# Revit family: BC_Hitachi_RAS-8-12FSXNME_LOD400
name_source: partatom
category: Equipement de génie climatique
revit_build: Autodesk Revit 2017 (Build: 20160225_1515(x64)
units: mm (PartAtom-declared; Revit-internal decimal feet)

## family parameters
Basée sur le plan de construction = Non
Cote de connecteur circulaire = Utiliser le diamètre
Couper avec des vides une fois chargée = Non
Numéro OmniClass = 23.75.00.00
Partagée = Non
Point de calcul de pièce = Non
Titre OmniClass = Climate Control (HVAC)
Toujours verticalement = Oui
Type d'élément = Normal

## types (3) — shared parameters
Approximate Packing Volume = 1.03 m³
Color = Natural Grey (1.0Y8.5/0.5)
Compressor Quantity = 1
Compressor Type = Hermetic (Scroll)
Condenser Fan Quantity = 2
Condenser Fan Type = Propeller Fan
Fabricant = Hitachi Air Conditioning Europe SAS
Flow Control = Micro-Computer control expansion valve
Frequency = 50 Hz
Heat Exchanger = Multi Pass Cross - Finned Tube
Modèle = Set Free Mini - RAS-8-12 FSXNME
Motor - Number of Poles = 6
Nominal Static Pressure = 30.0 Pa
Nominal Voltage = 400 V
Number of Poles = 3
Overall Depth = 390.00 mm
Overall Height = 1650.00 mm
Overall Width = 1100.00 mm
Packing dimensions (H x W x D) = 1787 mm x 1151 mm x 500 mm
Refrigerant Type = R410A
Refrigerant charge before shipment = 4.20 kg
Refrigeration Oil Charge = 6
Refrigeration Oil Type = FVC68D

## per-type parameters (varying)
| type | Compressor Model | Cooling Capacity | Gas Diameter | Gross Weight | Heating Capacity | Liquid Diameter | Motor power | Net Weight | Nominal Air Flow | Sound Pressure Level (night mode) | Sound level |
| RAS-8FSXNME | AA50PHD | 22 kW | 19.05 mm | 197.00 kg | 25 kW | 9.52 mm | 3 kW | 188.00 kg | 9900.0 m³/h | 55 (50) | 76 |
| RAS-10FSXNME | DB65PHD | 28 kW | 22.20 mm | 203.00 kg | 32 kW | 9.52 mm | 4 kW | 194.00 kg | 11100.0 m³/h | 59 (53) | 77 |
| RAS-12FSXNME | DC80PHD | 34 kW | 25.40 mm | 205.00 kg | 38 kW | 12.70 mm | 5 kW | 196.00 kg | 11100.0 m³/h | 60 (53) | 77 |

note: column(s) folded — value = type name in every type: Commentaires du type, Designation, Reference

## geometry (parser evidence)
native form markers: Blend x2
no freeform markers — native parametric forms only
